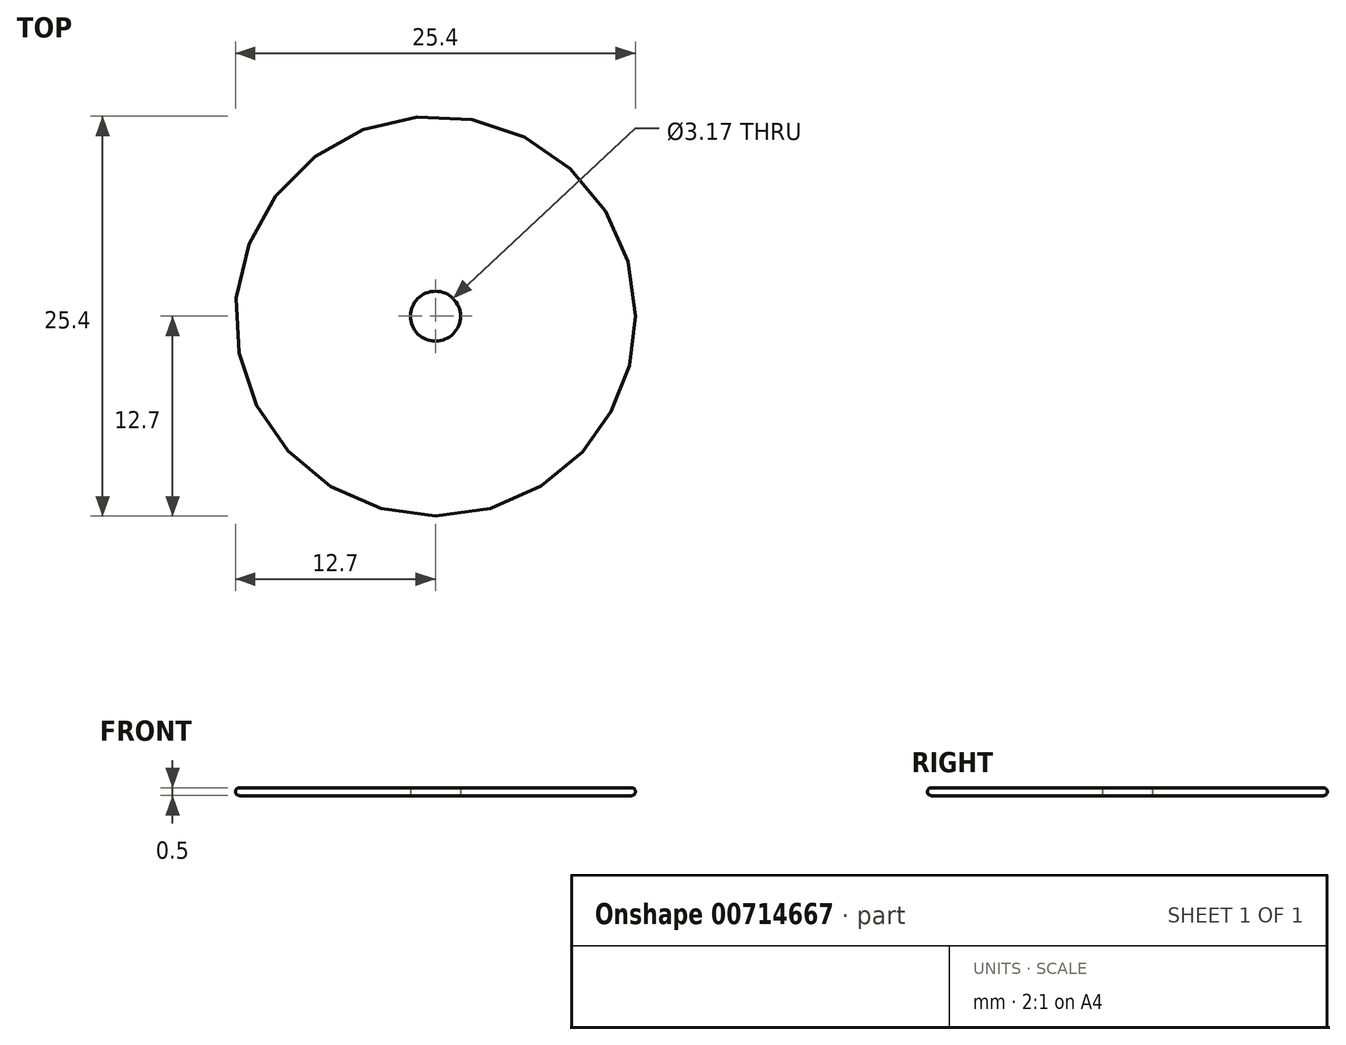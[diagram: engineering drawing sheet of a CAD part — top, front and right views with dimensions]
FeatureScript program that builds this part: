
annotation { "Feature Type Name" : "Feature", "Feature Type Description" : "" }
export const myFeature = defineFeature(function(context is Context, id is Id, definition is map)
    precondition{}
    {
        {
            var Q0;
            Q0=qCreatedBy(makeId("Top.planeOp"),FACE);
            var sketch = newSketch(context, id + "F0", { "sketchPlane" : qUnion([Q0])});
            skCircle(sketch, "E0", {"center": v(0, 0) * mm, "radius": 1.59 * mm});
            skCircle(sketch, "E1", {"center": v(0, 0) * mm, "radius": 12.7 * mm});
            skSolve(sketch);
        }
        {
            var Q0;
            Q0=makeQuery(id+"F0.imprint","IMPRINT",FACE,{"disambiguationData":[TD([[makeQuery(id+"F0.imprint","IMPRINT",EDGE,{"derivedFrom":sQuery(id+"F0.wireOp",EDGE,"E0")}),-1.0]])]});
            extrude(context, id + "F1", {"entities" : qUnion([Q0]), "depth" : 0.5 * mm, "offsetDistance" : 25.4 * mm, "symmetric" : true});
        }
        {
            var Q0;
            Q0=makeQuery(id+"F1.opExtrude","CAP_EDGE",EDGE,{"disambiguationData":[OSD([sQuery(id+"F0.wireOp",EDGE,"E1")])],"isStart":false});
            var Q1;
            Q1=makeQuery(id+"F1.opExtrude","CAP_EDGE",EDGE,{"disambiguationData":[OSD([sQuery(id+"F0.wireOp",EDGE,"E1")])],"isStart":true});
            fillet(context, id + "F2", {"entities" : qUnion([Q0, Q1]), "radius" : 0.25 * mm, "tangentPropagation" : true, "allowEdgeOverflow" : false});
        }
    });
